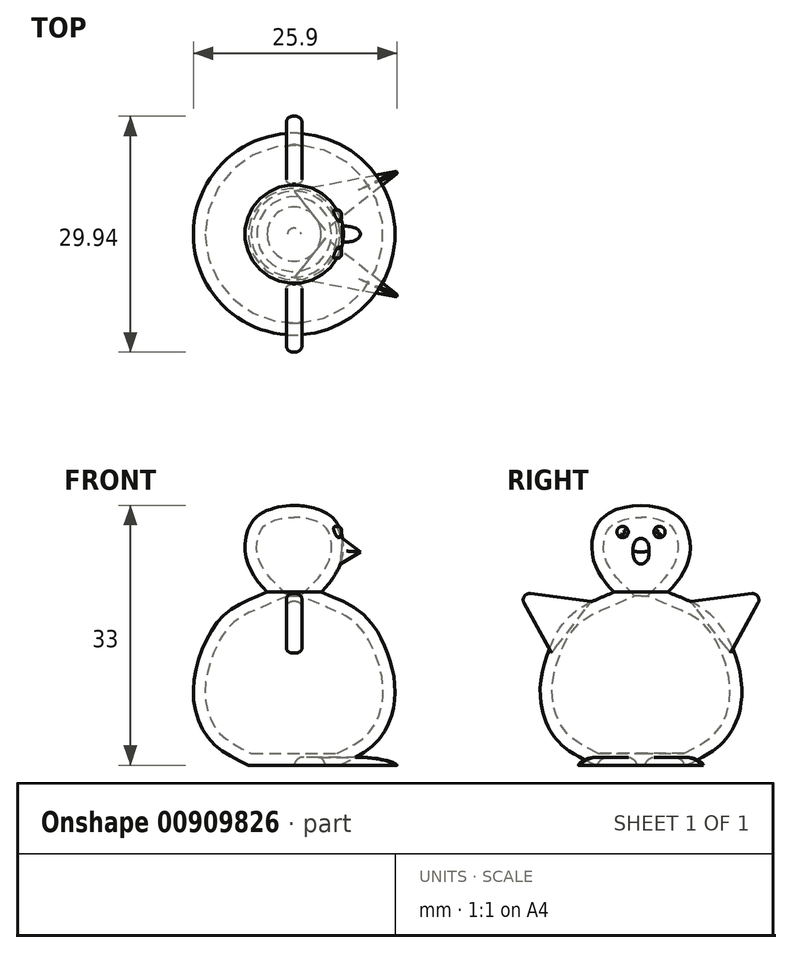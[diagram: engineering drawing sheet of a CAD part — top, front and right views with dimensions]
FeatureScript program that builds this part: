
annotation { "Feature Type Name" : "Feature", "Feature Type Description" : "" }
export const myFeature = defineFeature(function(context is Context, id is Id, definition is map)
    precondition{}
    {
        {
            var Q0;
            Q0=qCreatedBy(makeId("Front.planeOp"),FACE);
            var sketch = newSketch(context, id + "F0", { "sketchPlane" : qUnion([Q0])});
            skLineSegment(sketch, "E0", {"start": v(0, 0) * mm, "end": v(0, -22) * mm});
            skLineSegment(sketch, "E1", {"start": v(0, 0) * mm, "end": v(3.43, 0) * mm});
            skLineSegment(sketch, "E2", {"start": v(0, -22) * mm, "end": v(5.8, -22) * mm});
            skFitSpline(sketch, "E3", {"points": [v(3.43, 0) * mm, v(8.54, -2.6) * mm, v(11.74, -7.46) * mm, v(12.77, -13.65) * mm, v(10.57, -18.92) * mm, v(5.8, -22) * mm], "startDerivative": vector(26.68, -11.54) * mm, "endDerivative": vector(-27.31, -13.18) * mm});
            skLineSegment(sketch, "E4", {"start": v(0, 0) * mm, "end": v(0, 11) * mm});
            skFitSpline(sketch, "E5", {"points": [v(3.43, 0) * mm, v(5.89, 3.61) * mm, v(6.16, 6.75) * mm, v(4.68, 9.62) * mm, v(0, 11) * mm], "startDerivative": vector(12.12, 12.08) * mm, "endDerivative": vector(-18.52, 0) * mm});
            skSolve(sketch);
        }
        {
            var Q0;
            Q0 = qSketchRegion(id + "F0", true);
            var Q1;
            Q1=sQuery(id+"F0.wireOp",EDGE,"E4");
            revolve(context, id + "F1", {"surfaceOperationType" : NewSurfaceOperationType.NEW, "entities" : qUnion([Q0]), "axis" : qUnion([Q1]), "revolveType" : RevolveType.FULL});
        }
        {
            var Q0;
            Q0=qCreatedBy(makeId("Front.planeOp"),FACE);
            var sketch = newSketch(context, id + "F2", { "sketchPlane" : qUnion([Q0])});
            skLineSegment(sketch, "E6", {"start": v(6.16, 6.8) * mm, "end": v(8.42, 5.11) * mm});
            skLineSegment(sketch, "E7", {"start": v(8.42, 5.11) * mm, "end": v(5.88, 3.57) * mm});
            skLineSegment(sketch, "E8", {"start": v(5.88, 3.57) * mm, "end": v(6.16, 6.8) * mm});
            skSolve(sketch);
        }
        {
            var Q0;
            Q0 = qSketchRegion(id + "F2", true);
            extrude(context, id + "F3", {"entities" : qUnion([Q0]), "endBound" : BoundingType.SYMMETRIC, "depth" : 2 * mm, "offsetDistance" : 25 * mm});
        }
        {
            var Q0;
            Q0=qCreatedBy(makeId("Right.planeOp"),FACE);
            var sketch = newSketch(context, id + "F4", { "sketchPlane" : qUnion([Q0])});
            skLineSegment(sketch, "E9", {"start": v(6.34, -1.22) * mm, "end": v(15.63, 0) * mm});
            skLineSegment(sketch, "E10", {"start": v(15.63, 0) * mm, "end": v(11.38, -7.74) * mm});
            skLineSegment(sketch, "E11", {"start": v(11.38, -7.74) * mm, "end": v(6.34, -1.22) * mm});
            skSolve(sketch);
        }
        {
            var Q0;
            Q0 = qSketchRegion(id + "F4", true);
            extrude(context, id + "F5", {"entities" : qUnion([Q0]), "endBound" : BoundingType.SYMMETRIC, "depth" : 2 * mm, "offsetDistance" : 25 * mm});
        }
        {
            var Q0;
            Q0=makeQuery(id+"F5.opExtrude","SWEPT_BODY",BODY,{"disambiguationData":[OSD([sQuery(id+"F4.wireOp",EDGE,"E9"),sQuery(id+"F4.wireOp",EDGE,"E10"),sQuery(id+"F4.wireOp",EDGE,"E11")])]});
            var Q1;
            Q1=qCreatedBy(makeId("Front.planeOp"),FACE);
            mirror(context, id + "F6", {"entities" : qUnion([Q0]), "mirrorPlane" : qUnion([Q1])});
        }
        {
            var Q0;
            Q0=qCreatedBy(makeId("Top.planeOp"),FACE);
            var sketch = newSketch(context, id + "F7", { "sketchPlane" : qUnion([Q0])});
            skLineSegment(sketch, "E12", {"start": v(0, -5.53) * mm, "end": v(13.57, -8.1) * mm});
            skLineSegment(sketch, "E13", {"start": v(13.57, -8.1) * mm, "end": v(3.96, -0.5) * mm});
            skLineSegment(sketch, "E14", {"start": v(3.96, -0.5) * mm, "end": v(0, -5.53) * mm});
            skSolve(sketch);
        }
        {
            var Q0;
            Q0 = qSketchRegion(id + "F7", true);
            extrude(context, id + "F8", {"entities" : qUnion([Q0]), "oppositeDirection" : true, "depth" : 22 * mm, "hasOffset" : true, "offsetDistance" : 30 * mm, "hasSecondDirection" : true, "secondDirectionOppositeDirection" : true, "secondDirectionDepth" : 21 * mm});
        }
        {
            var Q0;
            Q0=makeQuery(id+"F8.opExtrude","SWEPT_BODY",BODY,{"disambiguationData":[OSD([sQuery(id+"F7.wireOp",EDGE,"E12"),sQuery(id+"F7.wireOp",EDGE,"E13"),sQuery(id+"F7.wireOp",EDGE,"E14")])]});
            var Q1;
            Q1=qCreatedBy(makeId("Front.planeOp"),FACE);
            mirror(context, id + "F9", {"entities" : qUnion([Q0]), "mirrorPlane" : qUnion([Q1])});
        }
        {
            var Q0;
            Q0=makeQuery(id+"F3.opExtrude","CAP_EDGE",EDGE,{"disambiguationData":[OSD([sQuery(id+"F2.wireOp",EDGE,"E6")])],"isStart":false});
            var Q1;
            Q1=makeQuery(id+"F3.opExtrude","CAP_EDGE",EDGE,{"disambiguationData":[OSD([sQuery(id+"F2.wireOp",EDGE,"E7")])],"isStart":false});
            var Q2;
            Q2=makeQuery(id+"F3.opExtrude","CAP_EDGE",EDGE,{"disambiguationData":[OSD([sQuery(id+"F2.wireOp",EDGE,"E7")])],"isStart":true});
            var Q3;
            Q3=makeQuery(id+"F3.opExtrude","CAP_EDGE",EDGE,{"disambiguationData":[OSD([sQuery(id+"F2.wireOp",EDGE,"E6")])],"isStart":true});
            fillet(context, id + "F10", {"entities" : qUnion([Q0, Q1, Q2, Q3]), "radius" : 1 * mm, "tangentPropagation" : true, "allowEdgeOverflow" : false});
        }
        {
            var Q0;
            Q0=makeQuery(id+"F5.opExtrude","SWEPT_EDGE",EDGE,{"disambiguationData":[OSD([sQuery(id+"F4.wireOp",EDGE,"E9"),sQuery(id+"F4.wireOp",EDGE,"E10")])]});
            var Q1;
            Q1=makeQuery(id+"F6.opPattern","COPY",EDGE,{"derivedFrom":makeQuery(id+"F5.opExtrude","SWEPT_EDGE",EDGE,{"disambiguationData":[OSD([sQuery(id+"F4.wireOp",EDGE,"E9"),sQuery(id+"F4.wireOp",EDGE,"E10")])]}),"instanceName":"1"});
            var Q2;
            Q2=makeQuery(id+"F5.opExtrude","CAP_EDGE",EDGE,{"disambiguationData":[OSD([sQuery(id+"F4.wireOp",EDGE,"E9")])],"isStart":false});
            var Q3;
            Q3=makeQuery(id+"F5.opExtrude","CAP_EDGE",EDGE,{"disambiguationData":[OSD([sQuery(id+"F4.wireOp",EDGE,"E9")])],"isStart":true});
            var Q4;
            Q4=makeQuery(id+"F5.opExtrude","CAP_EDGE",EDGE,{"disambiguationData":[OSD([sQuery(id+"F4.wireOp",EDGE,"E10")])],"isStart":false});
            var Q5;
            Q5=makeQuery(id+"F6.opPattern","COPY",EDGE,{"derivedFrom":makeQuery(id+"F5.opExtrude","CAP_EDGE",EDGE,{"disambiguationData":[OSD([sQuery(id+"F4.wireOp",EDGE,"E9")])],"isStart":false}),"instanceName":"1"});
            var Q6;
            Q6=makeQuery(id+"F6.opPattern","COPY",EDGE,{"derivedFrom":makeQuery(id+"F5.opExtrude","CAP_EDGE",EDGE,{"disambiguationData":[OSD([sQuery(id+"F4.wireOp",EDGE,"E9")])],"isStart":true}),"instanceName":"1"});
            var Q7;
            Q7=makeQuery(id+"F6.opPattern","COPY",EDGE,{"derivedFrom":makeQuery(id+"F5.opExtrude","CAP_EDGE",EDGE,{"disambiguationData":[OSD([sQuery(id+"F4.wireOp",EDGE,"E10")])],"isStart":false}),"instanceName":"1"});
            var Q8;
            Q8=makeQuery(id+"F5.opExtrude","CAP_EDGE",EDGE,{"disambiguationData":[OSD([sQuery(id+"F4.wireOp",EDGE,"E10")])],"isStart":true});
            var Q9;
            Q9=makeQuery(id+"F6.opPattern","COPY",EDGE,{"derivedFrom":makeQuery(id+"F5.opExtrude","CAP_EDGE",EDGE,{"disambiguationData":[OSD([sQuery(id+"F4.wireOp",EDGE,"E10")])],"isStart":true}),"instanceName":"1"});
            fillet(context, id + "F11", {"entities" : qUnion([Q0, Q1, Q2, Q3, Q4, Q5, Q6, Q7, Q8, Q9]), "radius" : 0.8 * mm, "tangentPropagation" : true, "allowEdgeOverflow" : false});
        }
        {
            var Q0;
            Q0=makeQuery(id+"F9.opPattern","COPY",EDGE,{"derivedFrom":makeQuery(id+"F8.opExtrude","CAP_EDGE",EDGE,{"disambiguationData":[OSD([sQuery(id+"F7.wireOp",EDGE,"E13")])],"isStart":true}),"instanceName":"1"});
            var Q1;
            Q1=makeQuery(id+"F9.opPattern","COPY",EDGE,{"derivedFrom":makeQuery(id+"F8.opExtrude","CAP_EDGE",EDGE,{"disambiguationData":[OSD([sQuery(id+"F7.wireOp",EDGE,"E12")])],"isStart":true}),"instanceName":"1"});
            var Q2;
            Q2=makeQuery(id+"F8.opExtrude","CAP_EDGE",EDGE,{"disambiguationData":[OSD([sQuery(id+"F7.wireOp",EDGE,"E13")])],"isStart":true});
            var Q3;
            Q3=makeQuery(id+"F8.opExtrude","CAP_EDGE",EDGE,{"disambiguationData":[OSD([sQuery(id+"F7.wireOp",EDGE,"E12")])],"isStart":true});
            fillet(context, id + "F12", {"entities" : qUnion([Q0, Q1, Q2, Q3]), "radius" : 1.5 * mm, "tangentPropagation" : true, "allowEdgeOverflow" : false});
        }
        {
            var Q0;
            Q0=makeQuery(id+"F12.opFillet","BLEND_EDGE",EDGE,{"blendedFrom":[makeQuery(id+"F9.opPattern","COPY",EDGE,{"derivedFrom":makeQuery(id+"F8.opExtrude","CAP_EDGE",EDGE,{"disambiguationData":[OSD([sQuery(id+"F7.wireOp",EDGE,"E12")])],"isStart":true}),"instanceName":"1"}),makeQuery(id+"F9.opPattern","COPY",EDGE,{"derivedFrom":makeQuery(id+"F8.opExtrude","CAP_EDGE",EDGE,{"disambiguationData":[OSD([sQuery(id+"F7.wireOp",EDGE,"E13")])],"isStart":true}),"instanceName":"1"})],"blendedInto":[]});
            var Q1;
            Q1=makeQuery(id+"F12.opFillet","BLEND_EDGE",EDGE,{"blendedFrom":[makeQuery(id+"F8.opExtrude","CAP_EDGE",EDGE,{"disambiguationData":[OSD([sQuery(id+"F7.wireOp",EDGE,"E12")])],"isStart":true}),makeQuery(id+"F8.opExtrude","CAP_EDGE",EDGE,{"disambiguationData":[OSD([sQuery(id+"F7.wireOp",EDGE,"E13")])],"isStart":true})],"blendedInto":[]});
            fillet(context, id + "F13", {"entities" : qUnion([Q0, Q1]), "radius" : .2 * mm, "tangentPropagation" : true, "allowEdgeOverflow" : false});
        }
        {
            var Q0;
            Q0=makeQuery(id+"F1.opRevolve","SWEPT_FACE",FACE,{"disambiguationData":[OSD([sQuery(id+"F0.wireOp",EDGE,"E3")])]});
            var Q1;
            Q1=makeQuery(id+"F1.opRevolve","SWEPT_FACE",FACE,{"disambiguationData":[OSD([sQuery(id+"F0.wireOp",EDGE,"E5")])]});
            var Q2;
            Q2=makeQuery(id+"F1.opRevolve","SWEPT_BODY",BODY,{"disambiguationData":[OSD([sQuery(id+"F0.wireOp",EDGE,"E0"),sQuery(id+"F0.wireOp",EDGE,"E2"),sQuery(id+"F0.wireOp",EDGE,"E3"),sQuery(id+"F0.wireOp",EDGE,"E4"),sQuery(id+"F0.wireOp",EDGE,"E5")])]});
            shell(context, id + "F14", {"isHollow" : true, "entities" : qUnion([Q0, Q1]), "parts" : qUnion([Q2]), "thickness" : 1.5 * mm});
        }
        {
            var Q0;
            Q0=qCreatedBy(makeId("Right.planeOp"),FACE);
            var sketch = newSketch(context, id + "F15", { "sketchPlane" : qUnion([Q0])});
            skCircle(sketch, "E15", {"center": v(2.34, 7.63) * mm, "radius": 0.72 * mm});
            skSolve(sketch);
        }
        {
            var Q0;
            Q0 = qSketchRegion(id + "F15", true);
            extrude(context, id + "F16", {"entities" : qUnion([Q0]), "depth" : 6 * mm, "offsetDistance" : 25 * mm, "hasSecondDirection" : true, "secondDirectionOppositeDirection" : false, "secondDirectionDepth" : 5 * mm});
        }
        {
            var Q0;
            Q0=makeQuery(id+"F16.opExtrude","SWEPT_BODY",BODY,{"disambiguationData":[OSD([sQuery(id+"F15.wireOp",EDGE,"E15")])]});
            var Q1;
            Q1=qCreatedBy(makeId("Front.planeOp"),FACE);
            mirror(context, id + "F17", {"operationType" : NewBodyOperationType.ADD, "entities" : qUnion([Q0]), "mirrorPlane" : qUnion([Q1])});
        }
        {
            var Q0;
            Q0=makeQuery(id+"F16.opExtrude","CAP_EDGE",EDGE,{"disambiguationData":[OSD([sQuery(id+"F15.wireOp",EDGE,"E15")])],"isStart":false});
            var Q1;
            Q1=makeQuery(id+"F17.opPattern","COPY",EDGE,{"derivedFrom":makeQuery(id+"F16.opExtrude","CAP_EDGE",EDGE,{"disambiguationData":[OSD([sQuery(id+"F15.wireOp",EDGE,"E15")])],"isStart":false}),"instanceName":"1"});
            fillet(context, id + "F18", {"entities" : qUnion([Q0, Q1]), "radius" : .5 * mm, "tangentPropagation" : true, "allowEdgeOverflow" : false});
        }
    });
